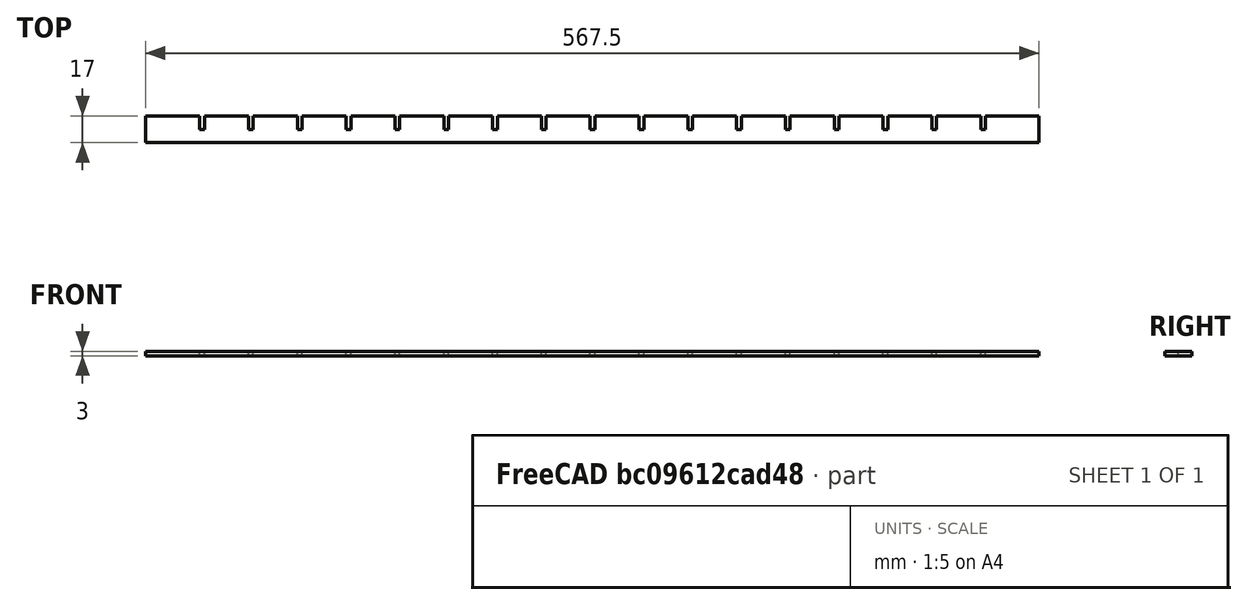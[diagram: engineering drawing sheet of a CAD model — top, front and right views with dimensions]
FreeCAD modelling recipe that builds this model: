
FCSTD DOCUMENT  (FreeCAD 0.16R6706 (Git))
Label: Leiste_lang_ohneAufnahme_9x
License: All rights reserved
LicenseURL: http://de.wikipedia.org/wiki/Alle_Rechte_vorbehalten
objects: Sketcher::SketchObject×1, PartDesign::Pad×1
note: 3 computed .brp shape members not serialized (recipe doc carries the construction recipe); baked Part::Feature solids carry a one-line shape summary decoded from their .brp

FEATURE [Sketcher::SketchObject] Sketch
  sketch-geometry (72):
    g0: LineSegment StartX=0 StartY=0 StartZ=0 EndX=0 EndY=17 EndZ=0
    g1: LineSegment StartX=0 StartY=17 StartZ=0 EndX=34.5 EndY=17 EndZ=0
    g2: LineSegment StartX=34.5 StartY=17 StartZ=0 EndX=34.5 EndY=8.5 EndZ=0
    g3: LineSegment StartX=34.5 StartY=8.5 StartZ=0 EndX=37.5 EndY=8.5 EndZ=0
    g4: LineSegment StartX=37.5 StartY=8.5 StartZ=0 EndX=37.5 EndY=17 EndZ=0
    g5: LineSegment StartX=37.5 StartY=17 StartZ=0 EndX=65.5 EndY=17 EndZ=0
    g6: LineSegment StartX=65.5 StartY=17 StartZ=0 EndX=65.5 EndY=8.5 EndZ=0
    g7: LineSegment StartX=65.5 StartY=8.5 StartZ=0 EndX=68.5 EndY=8.5 EndZ=0
    g8: LineSegment StartX=68.5 StartY=8.5 StartZ=0 EndX=68.5 EndY=17 EndZ=0
    g9: LineSegment StartX=68.5 StartY=17 StartZ=0 EndX=96.5 EndY=17 EndZ=0
    g10: LineSegment StartX=96.5 StartY=17 StartZ=0 EndX=96.5 EndY=8.5 EndZ=0
    g11: LineSegment StartX=96.5 StartY=8.5 StartZ=0 EndX=99.5 EndY=8.5 EndZ=0
    g12: LineSegment StartX=99.5 StartY=8.5 StartZ=0 EndX=99.5 EndY=17 EndZ=0
    g13: LineSegment StartX=99.5 StartY=17 StartZ=0 EndX=127.5 EndY=17 EndZ=0
    g14: LineSegment StartX=127.5 StartY=17 StartZ=0 EndX=127.5 EndY=8.5 EndZ=0
    g15: LineSegment StartX=127.5 StartY=8.5 StartZ=0 EndX=130.5 EndY=8.5 EndZ=0
    g16: LineSegment StartX=130.5 StartY=8.5 StartZ=0 EndX=130.5 EndY=17 EndZ=0
    g17: LineSegment StartX=130.5 StartY=17 StartZ=0 EndX=158.5 EndY=17 EndZ=0
    g18: LineSegment StartX=158.5 StartY=17 StartZ=0 EndX=158.5 EndY=8.5 EndZ=0
    g19: LineSegment StartX=158.5 StartY=8.5 StartZ=0 EndX=161.5 EndY=8.5 EndZ=0
    g20: LineSegment StartX=161.5 StartY=8.5 StartZ=0 EndX=161.5 EndY=17 EndZ=0
    g21: LineSegment StartX=161.5 StartY=17 StartZ=0 EndX=189.5 EndY=17 EndZ=0
    g22: LineSegment StartX=189.5 StartY=17 StartZ=0 EndX=189.5 EndY=8.5 EndZ=0
    g23: LineSegment StartX=189.5 StartY=8.5 StartZ=0 EndX=192.5 EndY=8.5 EndZ=0
    g24: LineSegment StartX=192.5 StartY=8.5 StartZ=0 EndX=192.5 EndY=17 EndZ=0
    g25: LineSegment StartX=192.5 StartY=17 StartZ=0 EndX=220.5 EndY=17 EndZ=0
    g26: LineSegment StartX=220.5 StartY=17 StartZ=0 EndX=220.5 EndY=8.5 EndZ=0
    g27: LineSegment StartX=220.5 StartY=8.5 StartZ=0 EndX=223.5 EndY=8.5 EndZ=0
    g28: LineSegment StartX=223.5 StartY=8.5 StartZ=0 EndX=223.5 EndY=17 EndZ=0
    g29: LineSegment StartX=223.5 StartY=17 StartZ=0 EndX=251.5 EndY=17 EndZ=0
    g30: LineSegment StartX=251.5 StartY=17 StartZ=0 EndX=251.5 EndY=8.5 EndZ=0
    g31: LineSegment StartX=251.5 StartY=8.5 StartZ=0 EndX=254.5 EndY=8.5 EndZ=0
    g32: LineSegment StartX=254.5 StartY=8.5 StartZ=0 EndX=254.5 EndY=17 EndZ=0
    g33: LineSegment StartX=254.5 StartY=17 StartZ=0 EndX=282.5 EndY=17 EndZ=0
    g34: LineSegment StartX=282.5 StartY=17 StartZ=0 EndX=282.5 EndY=8.5 EndZ=0
    g35: LineSegment StartX=282.5 StartY=8.5 StartZ=0 EndX=285.5 EndY=8.5 EndZ=0
    g36: LineSegment StartX=285.5 StartY=8.5 StartZ=0 EndX=285.5 EndY=17 EndZ=0
    g37: LineSegment StartX=285.5 StartY=17 StartZ=0 EndX=313.5 EndY=17 EndZ=0
    g38: LineSegment StartX=313.5 StartY=17 StartZ=0 EndX=313.5 EndY=8.5 EndZ=0
    g39: LineSegment StartX=313.5 StartY=8.5 StartZ=0 EndX=316.5 EndY=8.5 EndZ=0
    g40: LineSegment StartX=316.5 StartY=8.5 StartZ=0 EndX=316.5 EndY=17 EndZ=0
    g41: LineSegment StartX=316.5 StartY=17 StartZ=0 EndX=344.5 EndY=17 EndZ=0
    g42: LineSegment StartX=344.5 StartY=17 StartZ=0 EndX=344.5 EndY=8.5 EndZ=0
    g43: LineSegment StartX=344.5 StartY=8.5 StartZ=0 EndX=347.5 EndY=8.5 EndZ=0
    g44: LineSegment StartX=347.5 StartY=8.5 StartZ=0 EndX=347.5 EndY=17 EndZ=0
    g45: LineSegment StartX=347.5 StartY=17 StartZ=0 EndX=375.5 EndY=17 EndZ=0
    g46: LineSegment StartX=375.5 StartY=17 StartZ=0 EndX=375.5 EndY=8.5 EndZ=0
    g47: LineSegment StartX=375.5 StartY=8.5 StartZ=0 EndX=378.5 EndY=8.5 EndZ=0
    g48: LineSegment StartX=378.5 StartY=8.5 StartZ=0 EndX=378.5 EndY=17 EndZ=0
    g49: LineSegment StartX=378.5 StartY=17 StartZ=0 EndX=406.5 EndY=17 EndZ=0
    g50: LineSegment StartX=406.5 StartY=17 StartZ=0 EndX=406.5 EndY=8.5 EndZ=0
    g51: LineSegment StartX=406.5 StartY=8.5 StartZ=0 EndX=409.5 EndY=8.5 EndZ=0
    g52: LineSegment StartX=409.5 StartY=8.5 StartZ=0 EndX=409.5 EndY=17 EndZ=0
    g53: LineSegment StartX=409.5 StartY=17 StartZ=0 EndX=437.5 EndY=17 EndZ=0
    g54: LineSegment StartX=437.5 StartY=17 StartZ=0 EndX=437.5 EndY=8.5 EndZ=0
    g55: LineSegment StartX=437.5 StartY=8.5 StartZ=0 EndX=440.5 EndY=8.5 EndZ=0
    g56: LineSegment StartX=440.5 StartY=8.5 StartZ=0 EndX=440.5 EndY=17 EndZ=0
    g57: LineSegment StartX=440.5 StartY=17 StartZ=0 EndX=468.5 EndY=17 EndZ=0
    g58: LineSegment StartX=468.5 StartY=17 StartZ=0 EndX=468.5 EndY=8.5 EndZ=0
    g59: LineSegment StartX=468.5 StartY=8.5 StartZ=0 EndX=471.5 EndY=8.5 EndZ=0
    g60: LineSegment StartX=471.5 StartY=8.5 StartZ=0 EndX=471.5 EndY=17 EndZ=0
    g61: LineSegment StartX=471.5 StartY=17 StartZ=0 EndX=499.5 EndY=17 EndZ=0
    g62: LineSegment StartX=499.5 StartY=17 StartZ=0 EndX=499.5 EndY=8.5 EndZ=0
    g63: LineSegment StartX=499.5 StartY=8.5 StartZ=0 EndX=502.5 EndY=8.5 EndZ=0
    g64: LineSegment StartX=502.5 StartY=8.5 StartZ=0 EndX=502.5 EndY=17 EndZ=0
    g65: LineSegment StartX=502.5 StartY=17 StartZ=0 EndX=530.5 EndY=17 EndZ=0
    g66: LineSegment StartX=530.5 StartY=17 StartZ=0 EndX=530.5 EndY=8.5 EndZ=0
    g67: LineSegment StartX=530.5 StartY=8.5 StartZ=0 EndX=533.5 EndY=8.5 EndZ=0
    g68: LineSegment StartX=533.5 StartY=8.5 StartZ=0 EndX=533.5 EndY=17 EndZ=0
    g69: LineSegment StartX=533.5 StartY=17 StartZ=0 EndX=567.5 EndY=17 EndZ=0
    g70: LineSegment StartX=567.5 StartY=17 StartZ=0 EndX=567.5 EndY=0 EndZ=0
    g71: LineSegment StartX=567.5 StartY=0 StartZ=0 EndX=0 EndY=0 EndZ=0
  constraints (215):
    c: Coincident(g-1,g0)
    c: PointOnObject(g0,g-2)
    c: Coincident(g0,g1)
    c: Horizontal(g1)
    c: Coincident(g1,g2)
    c: Vertical(g2)
    c: Coincident(g2,g3)
    c: Horizontal(g3)
    c: Coincident(g3,g4)
    c: Vertical(g4)
    c: Coincident(g4,g5)
    c: Horizontal(g5)
    c: DistanceX(g2,g3) = 3
    c: DistanceX(g1,g5) = 31
    c: DistanceY(g2,g1) = 8.5
    c: Equal(g2,g4)
    c: Coincident(g5,g6)
    c: Vertical(g6)
    c: Coincident(g6,g7)
    c: Horizontal(g7)
    c: Coincident(g7,g8)
    c: Vertical(g8)
    c: Coincident(g8,g9)
    c: Horizontal(g9)
    c: Coincident(g9,g10)
    c: Vertical(g10)
    c: Coincident(g10,g11)
    c: Horizontal(g11)
    c: Coincident(g11,g12)
    c: Vertical(g12)
    c: Coincident(g12,g13)
    c: Horizontal(g13)
    c: Coincident(g13,g14)
    c: Vertical(g14)
    c: Coincident(g14,g15)
    c: Horizontal(g15)
    c: Coincident(g15,g16)
    c: Vertical(g16)
    c: Coincident(g16,g17)
    c: Horizontal(g17)
    c: Coincident(g17,g18)
    c: Vertical(g18)
    c: Coincident(g18,g19)
    c: Horizontal(g19)
    c: Coincident(g19,g20)
    c: Vertical(g20)
    c: Coincident(g20,g21)
    c: Horizontal(g21)
    c: Coincident(g21,g22)
    c: Vertical(g22)
    c: Coincident(g22,g23)
    c: Horizontal(g23)
    c: Coincident(g23,g24)
    c: Vertical(g24)
    c: Coincident(g24,g25)
    c: Horizontal(g25)
    c: Coincident(g25,g26)
    c: Vertical(g26)
    c: Coincident(g26,g27)
    c: Horizontal(g27)
    c: Coincident(g27,g28)
    c: Vertical(g28)
    c: Coincident(g28,g29)
    c: Horizontal(g29)
    c: Coincident(g29,g30)
    c: Vertical(g30)
    c: Coincident(g30,g31)
    c: Horizontal(g31)
    c: Coincident(g31,g32)
    c: Vertical(g32)
    c: Coincident(g32,g33)
    c: Horizontal(g33)
    c: Coincident(g33,g34)
    c: Vertical(g34)
    c: Coincident(g34,g35)
    c: Horizontal(g35)
    c: Coincident(g35,g36)
    c: Vertical(g36)
    c: Coincident(g36,g37)
    c: Horizontal(g37)
    c: Coincident(g37,g38)
    c: Vertical(g38)
    c: Coincident(g38,g39)
    c: Horizontal(g39)
    c: Coincident(g39,g40)
    c: Vertical(g40)
    c: Coincident(g40,g41)
    c: Horizontal(g41)
    c: Coincident(g41,g42)
    c: Vertical(g42)
    c: Coincident(g42,g43)
    c: Horizontal(g43)
    c: Coincident(g43,g44)
    c: Vertical(g44)
    c: Coincident(g44,g45)
    c: Horizontal(g45)
    c: Coincident(g45,g46)
    c: Vertical(g46)
    c: Coincident(g46,g47)
    c: Horizontal(g47)
    c: Coincident(g47,g48)
    c: Vertical(g48)
    c: Coincident(g48,g49)
    c: Horizontal(g49)
    c: Coincident(g49,g50)
    c: Vertical(g50)
    c: Coincident(g50,g51)
    c: Horizontal(g51)
    c: Coincident(g51,g52)
    c: Vertical(g52)
    c: Coincident(g52,g53)
    c: Horizontal(g53)
    c: Coincident(g53,g54)
    c: Vertical(g54)
    c: Coincident(g54,g55)
    c: Horizontal(g55)
    c: Coincident(g55,g56)
    c: Vertical(g56)
    c: Coincident(g56,g57)
    c: Horizontal(g57)
    c: Coincident(g57,g58)
    c: Vertical(g58)
    c: Coincident(g58,g59)
    c: Horizontal(g59)
    c: Coincident(g59,g60)
    c: Vertical(g60)
    c: Coincident(g60,g61)
    c: Horizontal(g61)
    c: Coincident(g61,g62)
    c: Vertical(g62)
    c: Coincident(g62,g63)
    c: Horizontal(g63)
    c: Coincident(g63,g64)
    c: Vertical(g64)
    c: Coincident(g64,g65)
    c: Horizontal(g65)
    c: Coincident(g65,g66)
    c: Vertical(g66)
    c: Coincident(g66,g67)
    c: Horizontal(g67)
    c: Coincident(g67,g68)
    c: Vertical(g68)
    c: Coincident(g68,g69)
    c: Horizontal(g69)
    c: Coincident(g69,g70)
    c: Vertical(g70)
    c: Coincident(g70,g71)
    c: Coincident(g71,g-1)
    c: Horizontal(g71)
    c: Equal(g4,g6)
    c: Equal(g6,g8)
    c: Equal(g8,g10)
    c: Equal(g10,g12)
    c: Equal(g12,g14)
    c: Equal(g14,g16)
    c: Equal(g16,g18)
    c: Equal(g18,g20)
    c: Equal(g20,g22)
    c: Equal(g22,g24)
    c: Equal(g24,g26)
    c: Equal(g26,g28)
    c: Equal(g28,g30)
    c: Equal(g30,g32)
    c: Equal(g32,g34)
    c: Equal(g34,g36)
    c: Equal(g36,g38)
    c: Equal(g38,g40)
    c: Equal(g40,g42)
    c: Equal(g42,g44)
    c: Equal(g44,g46)
    c: Equal(g46,g48)
    c: Equal(g48,g50)
    c: Equal(g50,g52)
    c: Equal(g52,g54)
    c: Equal(g54,g56)
    c: Equal(g56,g58)
    c: Equal(g58,g60)
    c: Equal(g60,g62)
    c: Equal(g62,g64)
    c: Equal(g64,g66)
    c: Equal(g66,g68)
    c: Equal(g5,g9)
    c: Equal(g9,g13)
    c: Equal(g3,g7)
    c: Equal(g7,g11)
    c: DistanceX(g-1,g70) = 567.5
    c: Equal(g13,g17)
    c: Equal(g17,g21)
    c: Equal(g11,g15)
    c: Equal(g15,g19)
    c: Equal(g21,g25)
    c: Equal(g25,g29)
    c: Equal(g19,g23)
    c: Equal(g23,g27)
    c: Equal(g29,g33)
    c: Equal(g33,g37)
    c: Equal(g37,g41)
    c: Equal(g27,g31)
    c: Equal(g31,g35)
    c: Equal(g35,g39)
    c: Equal(g41,g45)
    c: Equal(g45,g49)
    c: Equal(g39,g43)
    c: Equal(g43,g47)
    c: Equal(g49,g53)
    c: Equal(g53,g57)
    c: Equal(g47,g51)
    c: Equal(g51,g55)
    c: Equal(g57,g61)
    c: Equal(g61,g65)
    c: Equal(g55,g59)
    c: Equal(g59,g63)
    c: Equal(g63,g67)
    c: DistanceY(g-1,g0) = 17
    c: DistanceX(g0,g1) = 34.5
FEATURE [PartDesign::Pad] Pad
  Length = 3
  Length2 = 100
  Sketch = -> Sketch
  Type = 0
